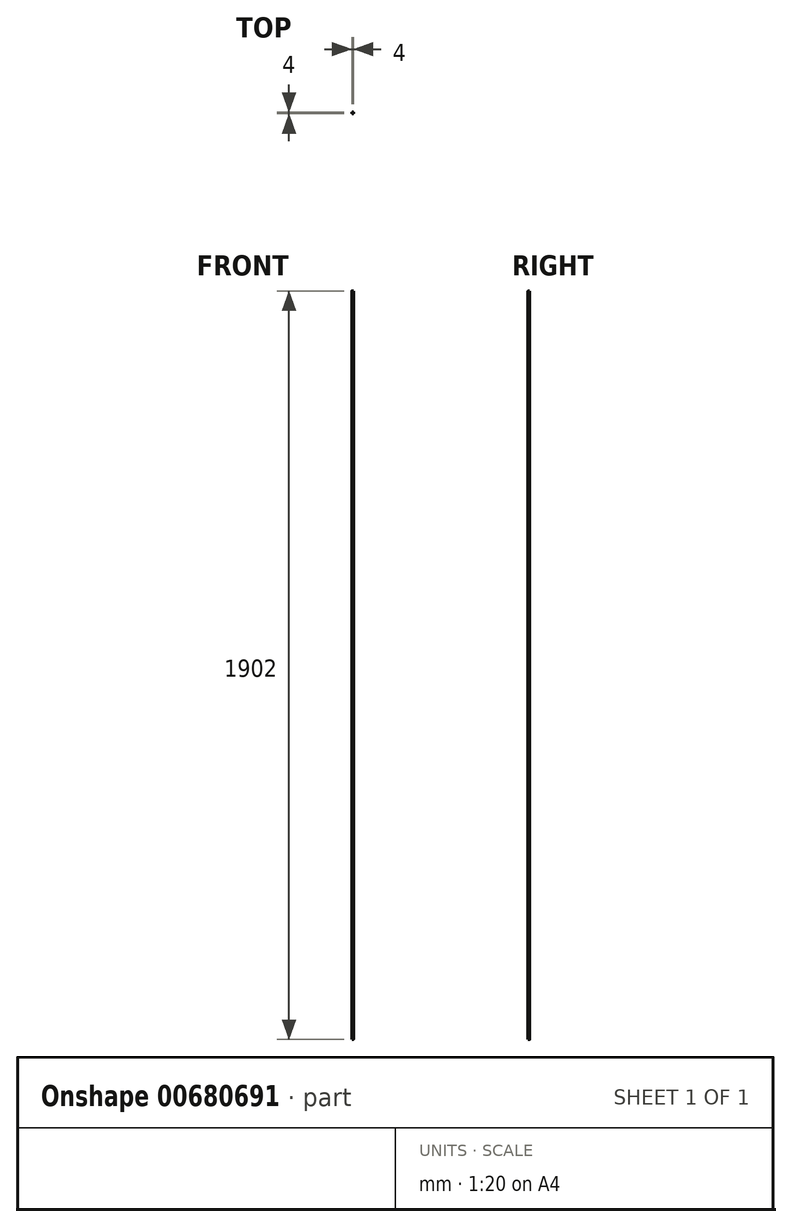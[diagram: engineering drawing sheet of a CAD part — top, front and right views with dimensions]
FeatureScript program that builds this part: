
annotation { "Feature Type Name" : "Feature", "Feature Type Description" : "" }
export const myFeature = defineFeature(function(context is Context, id is Id, definition is map)
    precondition{}
    {
        {
            var Q0;
            Q0=qCreatedBy(makeId("Top.planeOp"),FACE);
            var sketch = newSketch(context, id + "F0", { "sketchPlane" : qUnion([Q0])});
            skCircle(sketch, "E0", {"center": v(0, 0) * mm, "radius": 2 * mm});
            skSolve(sketch);
        }
        {
            var Q0;
            Q0=makeQuery(id+"F0.imprint","IMPRINT",FACE,{"disambiguationData":[TD([[makeQuery(id+"F0.imprint","IMPRINT",EDGE,{"derivedFrom":sQuery(id+"F0.wireOp",EDGE,"E0")}),1.0]])]});
            extrude(context, id + "F1", {"entities" : qUnion([Q0]), "depth" : 1902 * mm, "offsetDistance" : 25 * mm});
        }
    });
